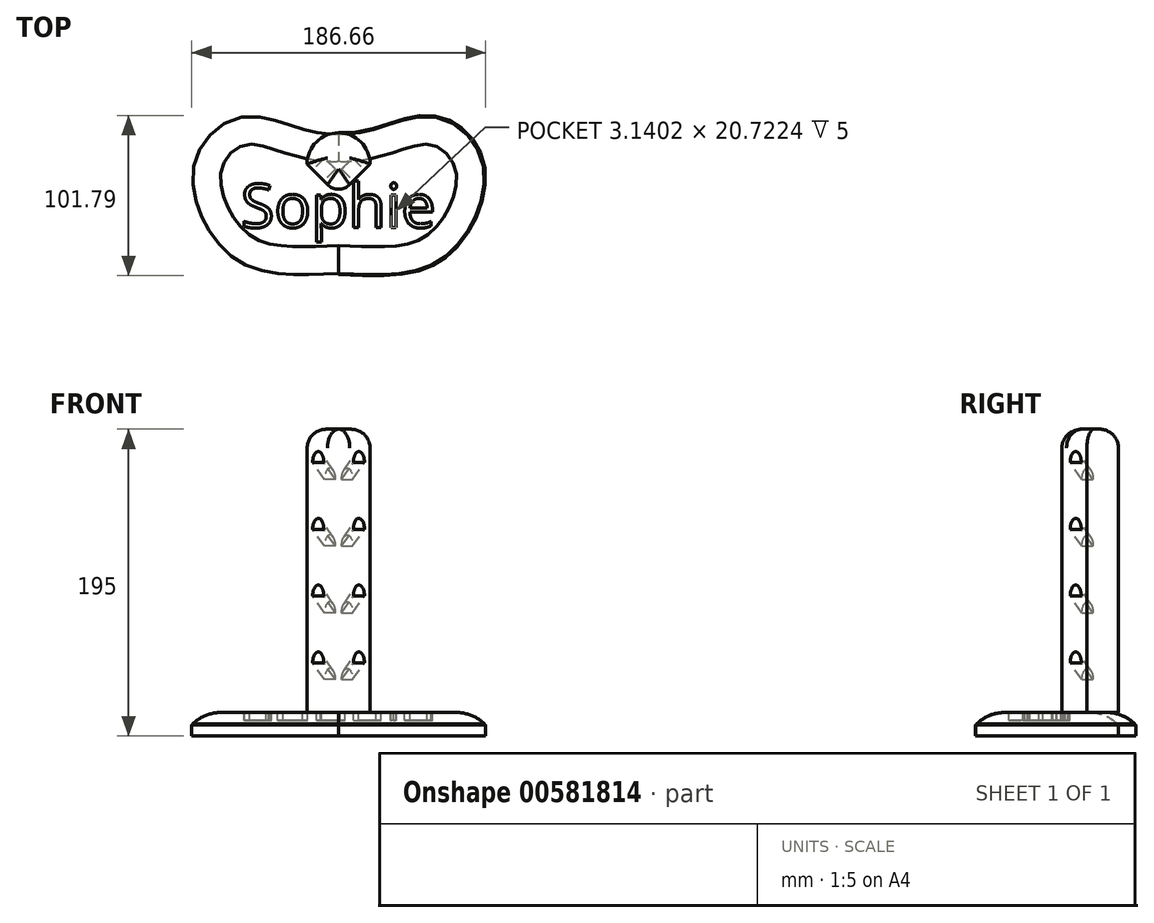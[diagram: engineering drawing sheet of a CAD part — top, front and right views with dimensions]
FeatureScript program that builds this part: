
annotation { "Feature Type Name" : "Feature", "Feature Type Description" : "" }
export const myFeature = defineFeature(function(context is Context, id is Id, definition is map)
    precondition{}
    {
        {
            var Q0;
            Q0=qCreatedBy(makeId("Top.planeOp"),FACE);
            var sketch = newSketch(context, id + "F0", { "sketchPlane" : qUnion([Q0])});
            skFitSpline(sketch, "E0", {"points": [v(0, 49.9) * mm, v(59.23, 60.83) * mm, v(92.65, 28.86) * mm, v(70.28, -27.51) * mm, v(0, -40.1) * mm], "startDerivative": vector(258.8, -15.57) * mm, "endDerivative": vector(-377.5, 19.2) * mm});
            skLineSegment(sketch, "E1", {"start": v(0, 49.9) * mm, "end": v(0, -40.1) * mm, "construction": true});
            skFitSpline(sketch, "E2.MirrorCS", {"points": [v(0, 49.9) * mm, v(-59.23, 60.83) * mm, v(-92.65, 28.86) * mm, v(-70.28, -27.51) * mm, v(0, -40.1) * mm], "startDerivative": vector(-258.8, -15.57) * mm, "endDerivative": vector(377.5, 19.2) * mm});
            skSolve(sketch);
        }
        {
            var Q0;
            Q0 = qSketchRegion(id + "F0", true);
            extrude(context, id + "F1", {"entities" : qUnion([Q0]), "depth" : 15 * mm, "offsetDistance" : 25 * mm});
        }
        {
            var Q0;
            Q0=makeQuery(id+"F1.opExtrude","CAP_EDGE",EDGE,{"disambiguationData":[OSD([sQuery(id+"F0.wireOp",EDGE,"E2.MirrorCS")])],"isStart":false});
            var Q1;
            Q1=makeQuery(id+"F1.opExtrude","CAP_EDGE",EDGE,{"disambiguationData":[OSD([sQuery(id+"F0.wireOp",EDGE,"E0")])],"isStart":false});
            chamfer(context, id + "F2", {"entities" : qUnion([Q0, Q1]), "width" : 8 * mm, "tangentPropagation" : true});
        }
        {
            var Q0;
            Q0=makeQuery(id+"F1.opExtrude","CAP_FACE",FACE,{"disambiguationData":[OSD([sQuery(id+"F0.wireOp",EDGE,"E0"),sQuery(id+"F0.wireOp",EDGE,"E2.MirrorCS")])],"isStart":false});
            fillet(context, id + "F3", {"entities" : qUnion([Q0]), "radius" : 25 * mm, "tangentPropagation" : true, "allowEdgeOverflow" : false});
        }
        {
            var Q0;
            Q0=makeQuery(id+"F1.opExtrude","CAP_FACE",FACE,{"disambiguationData":[OSD([sQuery(id+"F0.wireOp",EDGE,"E0"),sQuery(id+"F0.wireOp",EDGE,"E2.MirrorCS")])],"isStart":false});
            var sketch = newSketch(context, id + "F4", { "sketchPlane" : qUnion([Q0])});
            skArc(sketch, "E3", {"start": v(20, 29.9) * mm, "mid": v(0, 49.9) * mm, "end": v(-20, 29.9) * mm});
            skPoint(sketch, "E4.0", {"position": v(0, 49.9) * mm});
            skLineSegment(sketch, "E5", {"start": v(-45.08, 9.9) * mm, "end": v(40.04, 9.9) * mm, "construction": true});
            skLineSegment(sketch, "E6", {"start": v(0, 9.9) * mm, "end": v(20, 29.9) * mm});
            skLineSegment(sketch, "E7", {"start": v(0, 9.9) * mm, "end": v(-20, 29.9) * mm});
            skSolve(sketch);
        }
        {
            var Q0;
            {var subQ10=sQuery(id+"F4.wireOp",EDGE,"E3");Q0=makeQuery(id+"F4.imprint","IMPRINT",FACE,{"disambiguationData":[TD([[makeQuery(id+"F4.imprint","IMPRINT",EDGE,{"derivedFrom":subQ10}),1.0]])]});}
            var Q1;
            {var subQ0=sQuery(id+"F4.wireOp",EDGE,"E7");var subQ1=sQuery(id+"F4.wireOp",EDGE,"E6");var subQ2=makeQuery(id+"F4.imprint","INTERSECT",VERTEX,{"derivedFrom":[subQ1,subQ0]});Q1=makeQuery(id+"F4.imprint","IMPRINT",FACE,{"disambiguationData":[TD([[makeQuery(id+"F4.imprint","IMPRINT",EDGE,{"disambiguationData":[TD([[subQ2,-1.0]])],"derivedFrom":subQ1}),1.0]])]});}
            var Q2;
            Q2=makeQuery(id+"F1.opExtrude","CAP_FACE",FACE,{"disambiguationData":[OSD([sQuery(id+"F0.wireOp",EDGE,"E0"),sQuery(id+"F0.wireOp",EDGE,"E2.MirrorCS")])],"isStart":true});
            extrude(context, id + "F5", {"entities" : qUnion([Q0, Q1]), "operationType" : NewBodyOperationType.ADD, "endBound" : BoundingType.UP_TO_SURFACE, "oppositeDirection" : true, "depth" : 25 * mm, "endBoundEntityFace" : qUnion([Q2]), "offsetDistance" : 25 * mm});
        }
        {
            var Q0;
            Q0 = qSketchRegion(id + "F4", true);
            extrude(context, id + "F6", {"entities" : qUnion([Q0]), "operationType" : NewBodyOperationType.ADD, "depth" : 180 * mm, "offsetDistance" : 25 * mm});
        }
        {
            var Q0;
            Q0=makeQuery(id+"F6.opExtrude","CAP_EDGE",EDGE,{"disambiguationData":[OSD([sQuery(id+"F4.wireOp",EDGE,"E6")])],"isStart":false});
            cPlane(context, id + "F7", {"entities" : qUnion([Q0]), "cplaneType" : CPlaneType.LINE_ANGLE, "offset" : 25 * mm, "angle" : 45 * degree, "width" : 150 * mm, "height" : 150 * mm});
        }
        {
            var Q0;
            Q0=qCreatedBy(id+"F7.planeOp",FACE);
            var sketch = newSketch(context, id + "F8", { "sketchPlane" : qUnion([Q0])});
            skArc(sketch, "E8", {"start": v(-49.08, 121.86) * mm, "mid": v(-56.05, 123.06) * mm, "end": v(-57.24, 116.09) * mm});
            skLineSegment(sketch, "E9", {"start": v(-57.24, 116.09) * mm, "end": v(-49.08, 121.86) * mm});
            skLineSegment(sketch, "E10.0.0", {"start": v(19.83, 33.07) * mm, "end": v(-53.66, 137) * mm, "construction": true});
            skLineSegment(sketch, "E10.0.1", {"start": v(-53.66, 137) * mm, "end": v(-76.75, 120.67) * mm, "construction": true});
            skLineSegment(sketch, "E10.0.2", {"start": v(-76.75, 120.67) * mm, "end": v(-3.27, 16.74) * mm, "construction": true});
            skLineSegment(sketch, "E10.0.3", {"start": v(-3.27, 16.74) * mm, "end": v(19.83, 33.07) * mm, "construction": true});
            skLineSegment(sketch, "E11", {"start": v(-61.82, 131.22) * mm, "end": v(11.66, 27.3) * mm, "construction": true});
            skArc(sketch, "E12.1.0.0", {"start": v(-31.76, 97.37) * mm, "mid": v(-38.73, 98.56) * mm, "end": v(-39.92, 91.6) * mm});
            skLineSegment(sketch, "E12.1.0.1", {"start": v(-39.92, 91.6) * mm, "end": v(-31.76, 97.37) * mm});
            skArc(sketch, "E12.2.0.0", {"start": v(-14.44, 72.87) * mm, "mid": v(-21.4, 74.07) * mm, "end": v(-22.6, 67.1) * mm});
            skLineSegment(sketch, "E12.2.0.1", {"start": v(-22.6, 67.1) * mm, "end": v(-14.44, 72.87) * mm});
            skArc(sketch, "E13", {"start": v(2.88, 48.38) * mm, "mid": v(-4.09, 49.57) * mm, "end": v(-5.28, 42.6) * mm});
            skLineSegment(sketch, "E14", {"start": v(-5.28, 42.6) * mm, "end": v(2.88, 48.38) * mm});
            skSolve(sketch);
        }
        {
            var Q0;
            Q0=makeQuery(id+"F8.imprint","IMPRINT",FACE,{"disambiguationData":[TD([[makeQuery(id+"F8.imprint","IMPRINT",EDGE,{"derivedFrom":sQuery(id+"F8.wireOp",EDGE,"E8")}),1.0]])]});
            var Q1;
            Q1=makeQuery(id+"F8.imprint","IMPRINT",FACE,{"disambiguationData":[TD([[makeQuery(id+"F8.imprint","IMPRINT",EDGE,{"derivedFrom":sQuery(id+"F8.wireOp",EDGE,"E12.1.0.0")}),1.0]])]});
            var Q2;
            Q2=makeQuery(id+"F8.imprint","IMPRINT",FACE,{"disambiguationData":[TD([[makeQuery(id+"F8.imprint","IMPRINT",EDGE,{"derivedFrom":sQuery(id+"F8.wireOp",EDGE,"E12.2.0.0")}),1.0]])]});
            var Q3;
            Q3=makeQuery(id+"F8.imprint","IMPRINT",FACE,{"disambiguationData":[TD([[makeQuery(id+"F8.imprint","IMPRINT",EDGE,{"derivedFrom":sQuery(id+"F8.wireOp",EDGE,"E13")}),1.0]])]});
            extrude(context, id + "F9", {"entities" : qUnion([Q0, Q1, Q2, Q3]), "operationType" : NewBodyOperationType.REMOVE, "endBound" : BoundingType.UP_TO_NEXT, "oppositeDirection" : true, "depth" : 25 * mm, "hasOffset" : true, "offsetDistance" : 15 * mm, "offsetOppositeDirection" : true});
        }
        {
            var Q0;
            Q0=makeQuery(id+"F6.opExtrude","CAP_EDGE",EDGE,{"disambiguationData":[OSD([sQuery(id+"F4.wireOp",EDGE,"E7")])],"isStart":false});
            cPlane(context, id + "F10", {"entities" : qUnion([Q0]), "cplaneType" : CPlaneType.LINE_ANGLE, "offset" : 25 * mm, "angle" : 45 * degree, "oppositeDirection" : true, "width" : 150 * mm, "height" : 150 * mm});
        }
        {
            var Q0;
            Q0=qCreatedBy(id+"F10.planeOp",FACE);
            var sketch = newSketch(context, id + "F11", { "sketchPlane" : qUnion([Q0])});
            skLineSegment(sketch, "E15.0.1", {"start": v(-19.83, 33.07) * mm, "end": v(3.27, 16.74) * mm, "construction": true});
            skLineSegment(sketch, "E15.0.2", {"start": v(3.27, 16.74) * mm, "end": v(76.75, 120.67) * mm, "construction": true});
            skLineSegment(sketch, "E15.0.3", {"start": v(76.75, 120.67) * mm, "end": v(53.66, 137) * mm, "construction": true});
            skLineSegment(sketch, "E15.0.4", {"start": v(53.66, 137) * mm, "end": v(-19.83, 33.07) * mm, "construction": true});
            skLineSegment(sketch, "E16", {"start": v(61.82, 131.22) * mm, "end": v(-11.66, 27.3) * mm, "construction": true});
            skArc(sketch, "E17", {"start": v(57.24, 116.09) * mm, "mid": v(56.05, 123.06) * mm, "end": v(49.08, 121.86) * mm});
            skLineSegment(sketch, "E18", {"start": v(49.08, 121.86) * mm, "end": v(57.24, 116.09) * mm});
            skArc(sketch, "E19.1.0.0", {"start": v(39.92, 91.6) * mm, "mid": v(38.73, 98.56) * mm, "end": v(31.76, 97.37) * mm});
            skLineSegment(sketch, "E19.1.0.1", {"start": v(31.76, 97.37) * mm, "end": v(39.92, 91.6) * mm});
            skArc(sketch, "E19.2.0.0", {"start": v(22.6, 67.1) * mm, "mid": v(21.4, 74.07) * mm, "end": v(14.44, 72.87) * mm});
            skLineSegment(sketch, "E19.2.0.1", {"start": v(14.44, 72.87) * mm, "end": v(22.6, 67.1) * mm});
            skArc(sketch, "E20", {"start": v(5.28, 42.6) * mm, "mid": v(4.09, 49.57) * mm, "end": v(-2.88, 48.38) * mm});
            skLineSegment(sketch, "E21", {"start": v(-2.88, 48.38) * mm, "end": v(5.28, 42.6) * mm});
            skSolve(sketch);
        }
        {
            var Q0;
            Q0=makeQuery(id+"F11.imprint","IMPRINT",FACE,{"disambiguationData":[TD([[makeQuery(id+"F11.imprint","IMPRINT",EDGE,{"derivedFrom":sQuery(id+"F11.wireOp",EDGE,"E17")}),1.0]])]});
            var Q1;
            Q1=makeQuery(id+"F11.imprint","IMPRINT",FACE,{"disambiguationData":[TD([[makeQuery(id+"F11.imprint","IMPRINT",EDGE,{"derivedFrom":sQuery(id+"F11.wireOp",EDGE,"E19.1.0.0")}),1.0]])]});
            var Q2;
            Q2=makeQuery(id+"F11.imprint","IMPRINT",FACE,{"disambiguationData":[TD([[makeQuery(id+"F11.imprint","IMPRINT",EDGE,{"derivedFrom":sQuery(id+"F11.wireOp",EDGE,"E19.2.0.0")}),1.0]])]});
            var Q3;
            Q3=makeQuery(id+"F11.imprint","IMPRINT",FACE,{"disambiguationData":[TD([[makeQuery(id+"F11.imprint","IMPRINT",EDGE,{"derivedFrom":sQuery(id+"F11.wireOp",EDGE,"E20")}),1.0]])]});
            extrude(context, id + "F12", {"entities" : qUnion([Q0, Q1, Q2, Q3]), "operationType" : NewBodyOperationType.REMOVE, "endBound" : BoundingType.UP_TO_NEXT, "oppositeDirection" : true, "depth" : 25 * mm, "hasOffset" : true, "offsetDistance" : 15 * mm, "offsetOppositeDirection" : true});
        }
        {
            var Q0;
            Q0=makeQuery(id+"F6.opExtrude","SWEPT_EDGE",EDGE,{"disambiguationData":[OSD([sQuery(id+"F4.wireOp",EDGE,"E6"),sQuery(id+"F4.wireOp",EDGE,"E7")])]});
            fillet(context, id + "F13", {"entities" : qUnion([Q0]), "radius" : 10 * mm, "tangentPropagation" : true, "allowEdgeOverflow" : false});
        }
        {
            var Q0;
            Q0=makeQuery(id+"F1.opExtrude","CAP_FACE",FACE,{"disambiguationData":[OSD([sQuery(id+"F0.wireOp",EDGE,"E0"),sQuery(id+"F0.wireOp",EDGE,"E2.MirrorCS")])],"isStart":false});
            var sketch = newSketch(context, id + "F14", { "sketchPlane" : qUnion([Q0])});
            skText(sketch, "E22", { "text": "Sophie", "fontName": "OpenSans-Regular.ttf"});
            const initialGuessF14  = {"E22": [-0.06208, -0.01026, 1, 0, 0.02788]};
            skSetInitialGuess(sketch, initialGuessF14);
            skSolve(sketch);
        }
        {
            var Q0;
            Q0 = qSketchRegion(id + "F14", true);
            extrude(context, id + "F15", {"entities" : qUnion([Q0]), "operationType" : NewBodyOperationType.REMOVE, "oppositeDirection" : true, "depth" : 5 * mm, "offsetDistance" : 25 * mm});
        }
        {
            var Q0;
            Q0=makeQuery(id+"F6.opExtrude","CAP_FACE",FACE,{"disambiguationData":[OSD([sQuery(id+"F4.wireOp",EDGE,"E3"),sQuery(id+"F4.wireOp",EDGE,"E6"),sQuery(id+"F4.wireOp",EDGE,"E7")])],"isStart":false});
            fillet(context, id + "F16", {"entities" : qUnion([Q0]), "radius" : 12 * mm, "tangentPropagation" : true, "allowEdgeOverflow" : false});
        }
    });
